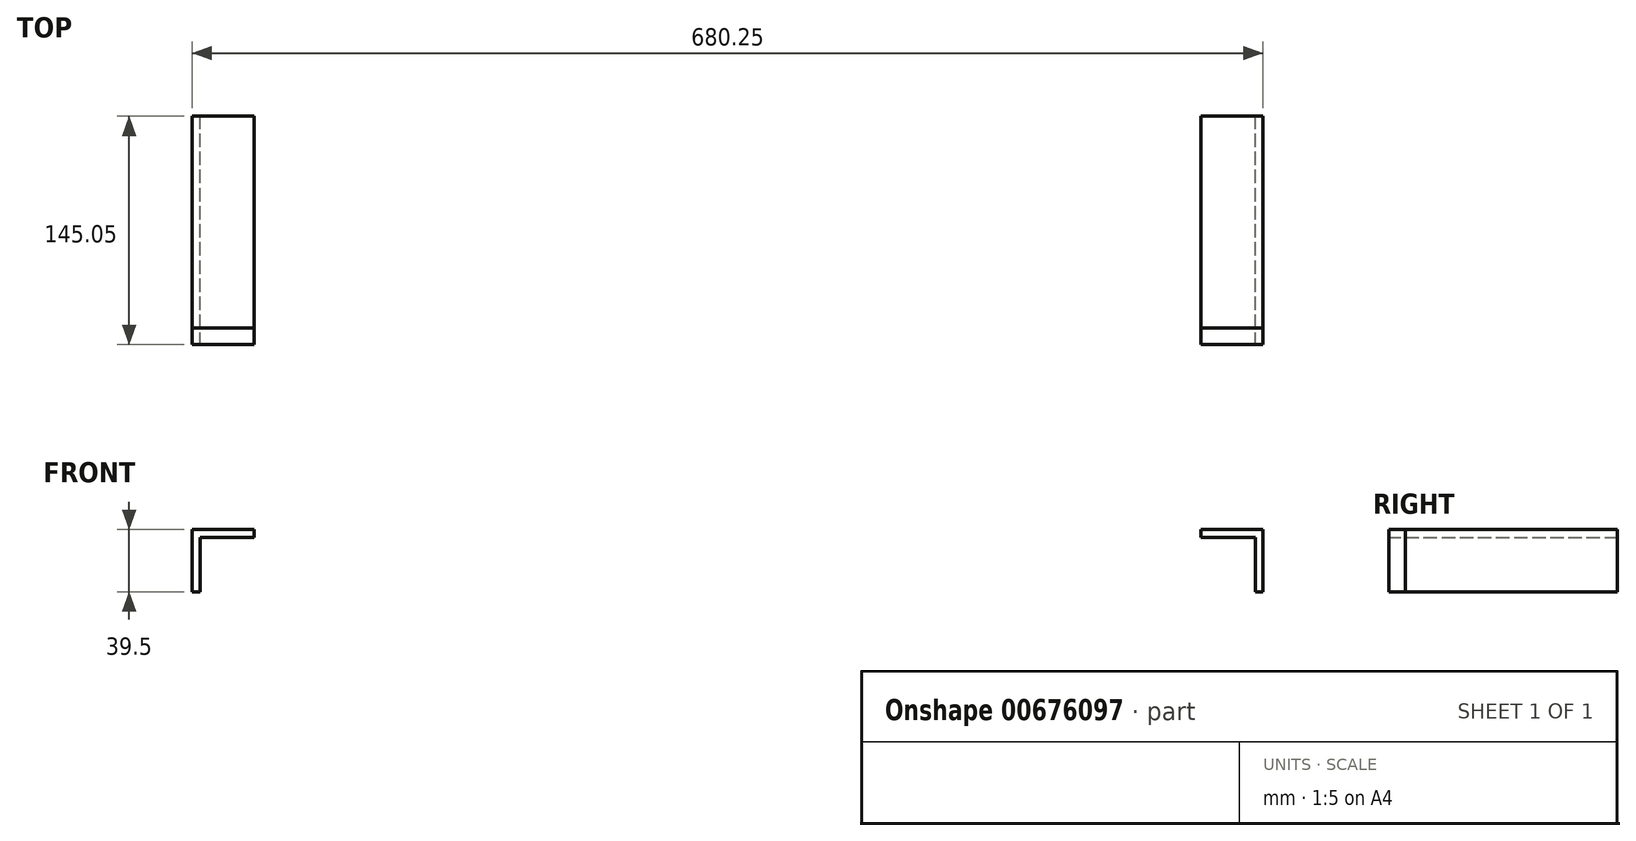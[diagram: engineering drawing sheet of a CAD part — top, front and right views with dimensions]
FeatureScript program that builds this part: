
annotation { "Feature Type Name" : "Feature", "Feature Type Description" : "" }
export const myFeature = defineFeature(function(context is Context, id is Id, definition is map)
    precondition{}
    {
        {
            var Q0;
            Q0=qCreatedBy(makeId("Front.planeOp"),FACE);
            var sketch = newSketch(context, id + "F0", { "sketchPlane" : qUnion([Q0])});
            skLineSegment(sketch, "E0", {"start": v(0, 0) * mm, "end": v(0, -39.5) * mm});
            skLineSegment(sketch, "E1", {"start": v(0, -39.5) * mm, "end": v(5, -39.5) * mm});
            skLineSegment(sketch, "E2", {"start": v(5, -39.5) * mm, "end": v(5, -5) * mm});
            skLineSegment(sketch, "E3", {"start": v(5, -5) * mm, "end": v(39.5, -5) * mm});
            skLineSegment(sketch, "E4", {"start": v(39.5, -5) * mm, "end": v(39.5, 0) * mm});
            skLineSegment(sketch, "E5", {"start": v(39.5, 0) * mm, "end": v(0, 0) * mm});
            skLineSegment(sketch, "E6", {"start": v(680.25, 0) * mm, "end": v(640.75, 0) * mm});
            skLineSegment(sketch, "E7", {"start": v(640.75, 0) * mm, "end": v(640.75, -5) * mm});
            skLineSegment(sketch, "E8", {"start": v(640.75, -5) * mm, "end": v(675.25, -5) * mm});
            skLineSegment(sketch, "E9", {"start": v(675.25, -5) * mm, "end": v(675.25, -39.5) * mm});
            skLineSegment(sketch, "E10", {"start": v(675.25, -39.5) * mm, "end": v(680.25, -39.5) * mm});
            skLineSegment(sketch, "E11", {"start": v(680.25, -39.5) * mm, "end": v(680.25, 0) * mm});
            skSolve(sketch);
        }
        {
            var Q0;
            Q0 = qSketchRegion(id + "F0", true);
            extrude(context, id + "F1", {"entities" : qUnion([Q0]), "depth" : 145.05 * mm, "offsetDistance" : 25 * mm});
        }
        {
            var Q0;
            Q0 = qSketchRegion(id + "F0", true);
            extrude(context, id + "F2", {"entities" : qUnion([Q0]), "depth" : 134.6 * mm, "offsetDistance" : 25 * mm});
        }
    });
